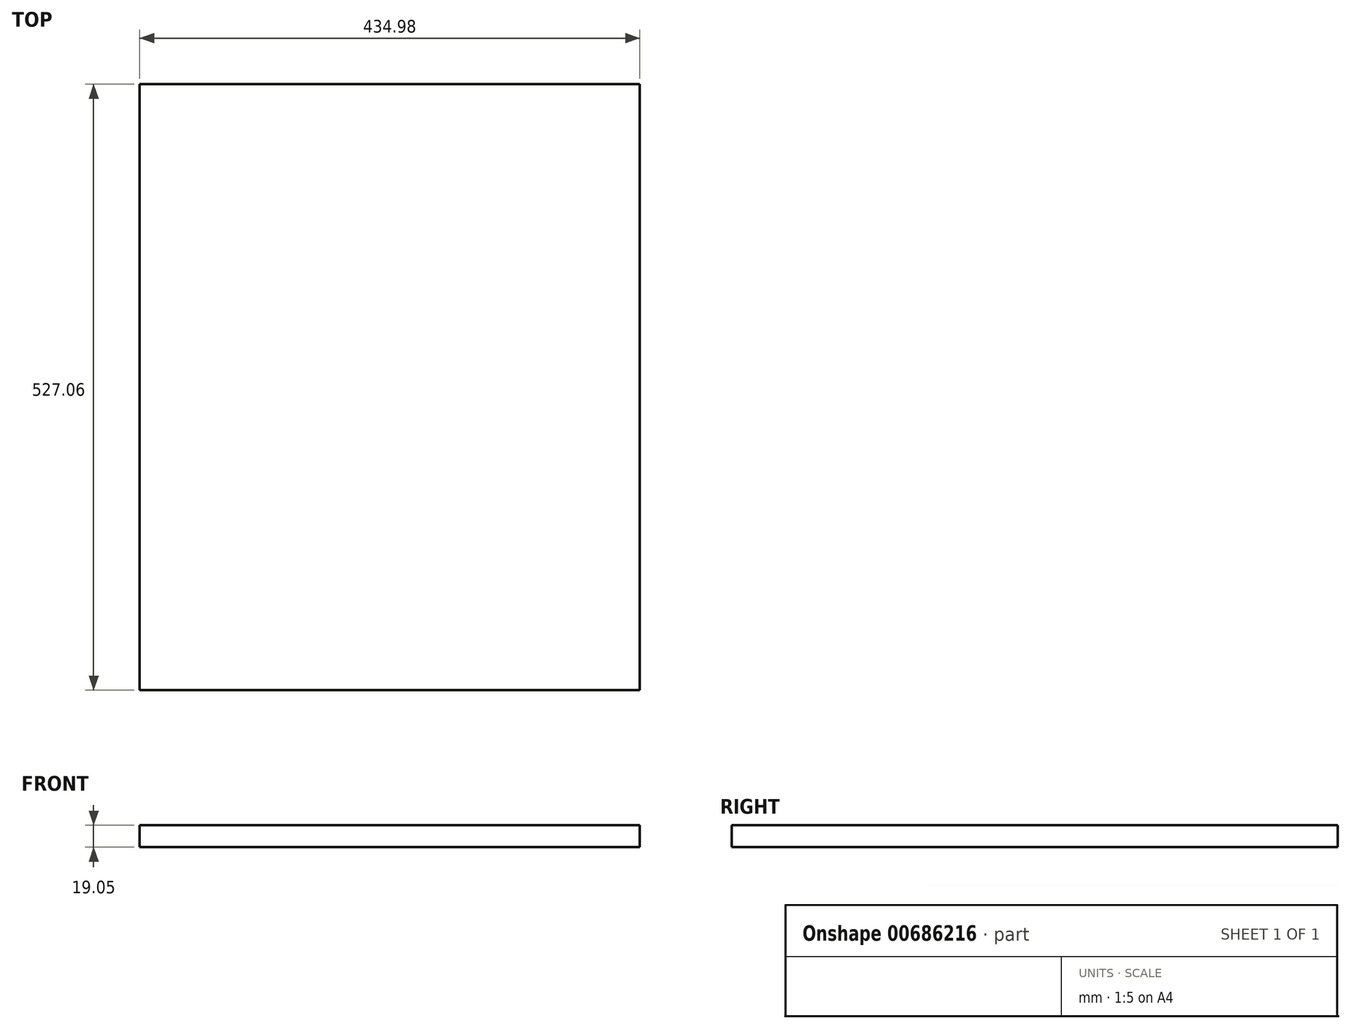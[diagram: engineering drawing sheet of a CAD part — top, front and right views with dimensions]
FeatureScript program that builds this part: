
annotation { "Feature Type Name" : "Feature", "Feature Type Description" : "" }
export const myFeature = defineFeature(function(context is Context, id is Id, definition is map)
    precondition{}
    {
        {
            var Q0;
            Q0=qCreatedBy(makeId("Top.planeOp"),FACE);
            var sketch = newSketch(context, id + "F0", { "sketchPlane" : qUnion([Q0])});
            skLineSegment(sketch, "E0.bottom", {"start": v(-217.49, 263.52) * mm, "end": v(217.49, 263.52) * mm});
            skLineSegment(sketch, "E0.top", {"start": v(-217.49, -263.53) * mm, "end": v(217.49, -263.53) * mm});
            skLineSegment(sketch, "E0.left", {"start": v(-217.49, 263.52) * mm, "end": v(-217.49, -263.53) * mm});
            skLineSegment(sketch, "E0.right", {"start": v(217.49, 263.52) * mm, "end": v(217.49, -263.53) * mm});
            skPoint(sketch, "E0.middle", {"position": v(0, 0) * mm});
            skSolve(sketch);
        }
        {
            var Q0;
            Q0 = qSketchRegion(id + "F0", true);
            extrude(context, id + "F1", {"entities" : qUnion([Q0]), "depth" : 19.05 * mm, "offsetDistance" : 25.4 * mm});
        }
    });
